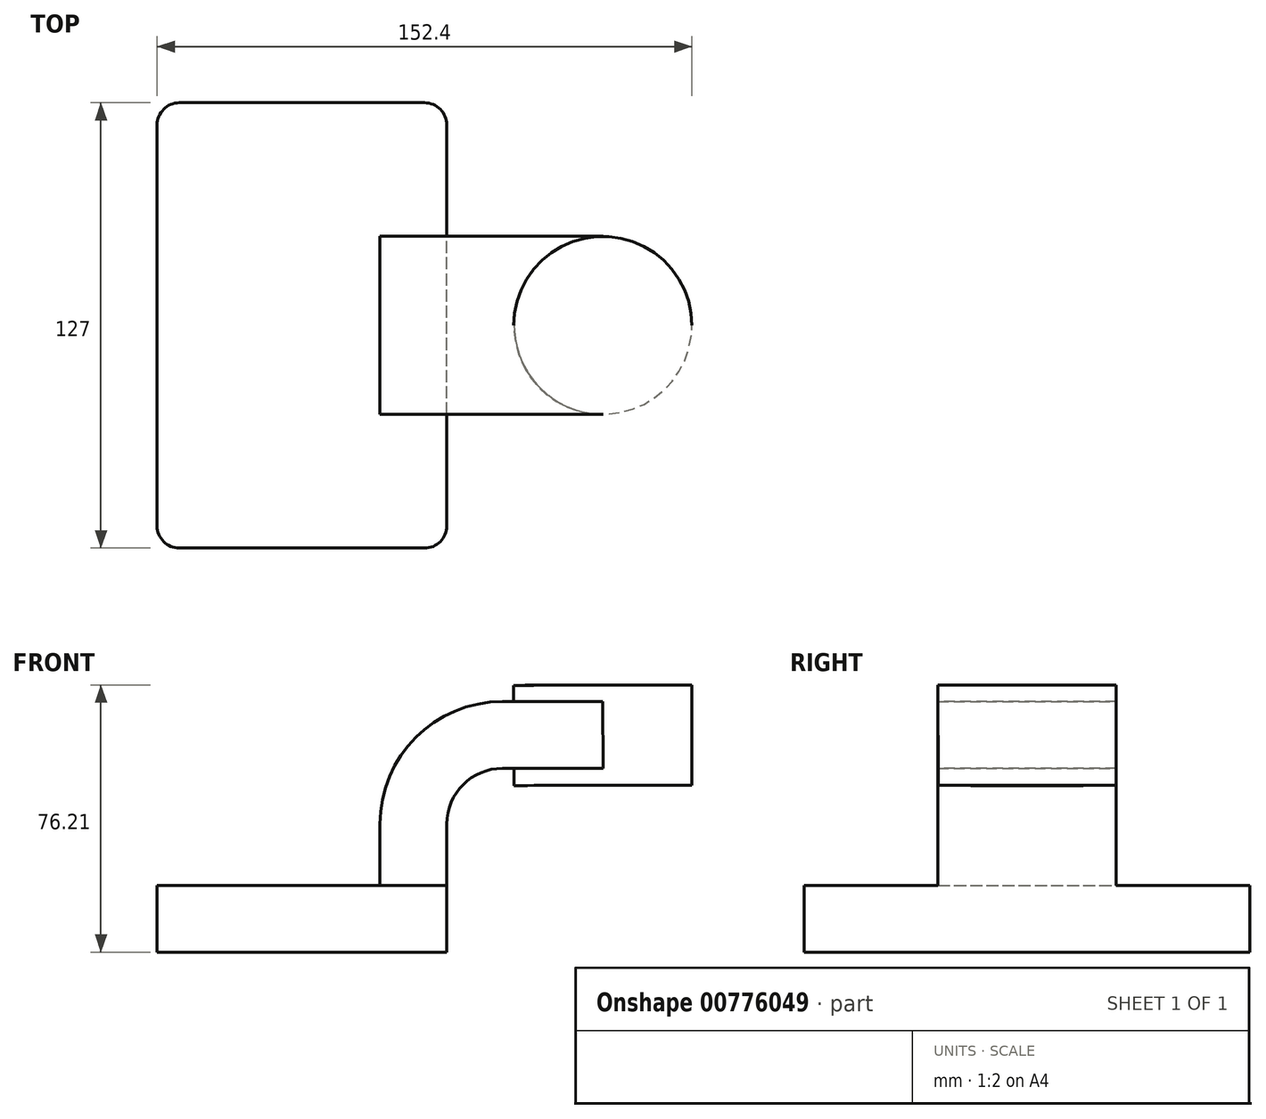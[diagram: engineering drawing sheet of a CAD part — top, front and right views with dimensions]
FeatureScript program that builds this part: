
annotation { "Feature Type Name" : "Feature", "Feature Type Description" : "" }
export const myFeature = defineFeature(function(context is Context, id is Id, definition is map)
    precondition{}
    {
        {
            var Q0;
            Q0=qCreatedBy(makeId("Front.planeOp"),FACE);
            var sketch = newSketch(context, id + "F0", { "sketchPlane" : qUnion([Q0])});
            skLineSegment(sketch, "E0.bottom", {"start": v(41.27, 9.53) * mm, "end": v(-41.28, 9.53) * mm});
            skLineSegment(sketch, "E0.top", {"start": v(41.28, -9.52) * mm, "end": v(-41.27, -9.52) * mm});
            skLineSegment(sketch, "E0.left", {"start": v(41.28, 9.53) * mm, "end": v(41.28, -9.52) * mm});
            skLineSegment(sketch, "E0.right", {"start": v(-41.28, 9.53) * mm, "end": v(-41.27, -9.52) * mm});
            skPoint(sketch, "E0.middle", {"position": v(0, 0) * mm});
            skLineSegment(sketch, "E1.bottom", {"start": v(111.12, 38.1) * mm, "end": v(60.32, 38.1) * mm});
            skLineSegment(sketch, "E1.top", {"start": v(111.12, 66.68) * mm, "end": v(60.32, 66.68) * mm});
            skLineSegment(sketch, "E1.left", {"start": v(111.12, 38.1) * mm, "end": v(111.12, 66.68) * mm});
            skLineSegment(sketch, "E1.right", {"start": v(60.32, 38.1) * mm, "end": v(60.32, 66.68) * mm});
            skPoint(sketch, "E1.middle", {"position": v(85.72, 52.39) * mm});
            skLineSegment(sketch, "E2", {"start": v(41.27, 9.53) * mm, "end": v(41.27, 27) * mm});
            skArc(sketch, "E3", {"start": v(41.27, 27) * mm, "mid": v(45.92, 38.23) * mm, "end": v(57.15, 42.88) * mm});
            skLineSegment(sketch, "E4", {"start": v(57.15, 42.88) * mm, "end": v(85.8, 42.88) * mm});
            skLineSegment(sketch, "E5.0", {"start": v(57.15, 61.93) * mm, "end": v(85.74, 61.93) * mm});
            skArc(sketch, "E5.1", {"start": v(22.23, 27) * mm, "mid": v(32.45, 51.7) * mm, "end": v(57.15, 61.93) * mm});
            skLineSegment(sketch, "E5.2", {"start": v(22.22, 9.53) * mm, "end": v(22.22, 27) * mm});
            skFitSpline(sketch, "E6", {"points": [v(-41.28, 9.52) * mm, v(57.15, 61.93) * mm], "startDerivative": vector(104.5, 18.3) * mm, "endDerivative": vector(220.73, -0.58) * mm});
            skLineSegment(sketch, "E7", {"start": v(85.72, 66.68) * mm, "end": v(85.8, 38.1) * mm});
            skSolve(sketch);
        }
        {
            var Q0;
            Q0=makeQuery(id+"F0.imprint","IMPRINT",FACE,{"disambiguationData":[TD([[makeQuery(id+"F0.imprint","IMPRINT",EDGE,{"derivedFrom":sQuery(id+"F0.wireOp",EDGE,"E0.top")}),-1.0]])]});
            extrude(context, id + "F1", {"entities" : qUnion([Q0]), "endBound" : BoundingType.SYMMETRIC, "depth" : 127 * mm, "offsetDistance" : 25.4 * mm});
        }
        {
            var Q0;
            {var subQ0=sQuery(id+"F0.wireOp",EDGE,"E4");var subQ1=sQuery(id+"F0.wireOp",EDGE,"E1.right");var subQ2=makeQuery(id+"F0.imprint","INTERSECT",VERTEX,{"derivedFrom":[subQ1,subQ0]});Q0=makeQuery(id+"F0.imprint","IMPRINT",FACE,{"disambiguationData":[TD([[makeQuery(id+"F0.imprint","IMPRINT",EDGE,{"disambiguationData":[TD([[subQ2,-1.0]])],"derivedFrom":subQ1}),-1.0]])]});}
            var Q1;
            {var subQ1=sQuery(id+"F0.wireOp",EDGE,"E2");Q1=makeQuery(id+"F0.imprint","IMPRINT",FACE,{"disambiguationData":[TD([[makeQuery(id+"F0.imprint","IMPRINT",EDGE,{"derivedFrom":subQ1}),1.0]])]});}
            extrude(context, id + "F2", {"entities" : qUnion([Q0, Q1]), "operationType" : NewBodyOperationType.ADD, "endBound" : BoundingType.SYMMETRIC, "depth" : 50.8 * mm, "offsetDistance" : 25.4 * mm});
        }
        {
            var Q0;
            Q0=makeQuery(id+"F0.imprint","IMPRINT",FACE,{"disambiguationData":[TD([[makeQuery(id+"F0.imprint","IMPRINT",EDGE,{"derivedFrom":sQuery(id+"F0.wireOp",EDGE,"E5.1")}),1.0]])]});
            extrude(context, id + "F3", {"entities" : qUnion([Q0]), "operationType" : NewBodyOperationType.ADD, "endBound" : BoundingType.SYMMETRIC, "depth" : 15.88 * mm, "offsetDistance" : 25.4 * mm});
        }
        {
            var Q0;
            {var subQ0=sQuery(id+"F0.wireOp",EDGE,"E1.left");Q0=makeQuery(id+"F0.imprint","IMPRINT",FACE,{"disambiguationData":[TD([[makeQuery(id+"F0.imprint","IMPRINT",EDGE,{"derivedFrom":subQ0}),1.0]])]});}
            var Q1;
            Q1=sQuery(id+"F0.wireOp",EDGE,"E7");
            revolve(context, id + "F4", {"operationType" : NewBodyOperationType.ADD, "surfaceOperationType" : NewSurfaceOperationType.NEW, "entities" : qUnion([Q0]), "axis" : qUnion([Q1]), "revolveType" : RevolveType.FULL});
        }
        {
            var Q0;
            Q0=makeQuery(id+"F1.opExtrude","CAP_EDGE",EDGE,{"disambiguationData":[OSD([sQuery(id+"F0.wireOp",EDGE,"E0.left")])],"isStart":false});
            var Q1;
            Q1=makeQuery(id+"F1.opExtrude","CAP_EDGE",EDGE,{"disambiguationData":[OSD([sQuery(id+"F0.wireOp",EDGE,"E0.right")])],"isStart":false});
            var Q2;
            Q2=makeQuery(id+"F1.opExtrude","CAP_EDGE",EDGE,{"disambiguationData":[OSD([sQuery(id+"F0.wireOp",EDGE,"E0.right")])],"isStart":true});
            var Q3;
            Q3=makeQuery(id+"F1.opExtrude","CAP_EDGE",EDGE,{"disambiguationData":[OSD([sQuery(id+"F0.wireOp",EDGE,"E0.left")])],"isStart":true});
            fillet(context, id + "F5", {"entities" : qUnion([Q0, Q1, Q2, Q3]), "radius" : 6.35 * mm, "tangentPropagation" : true, "allowEdgeOverflow" : false});
        }
    });
